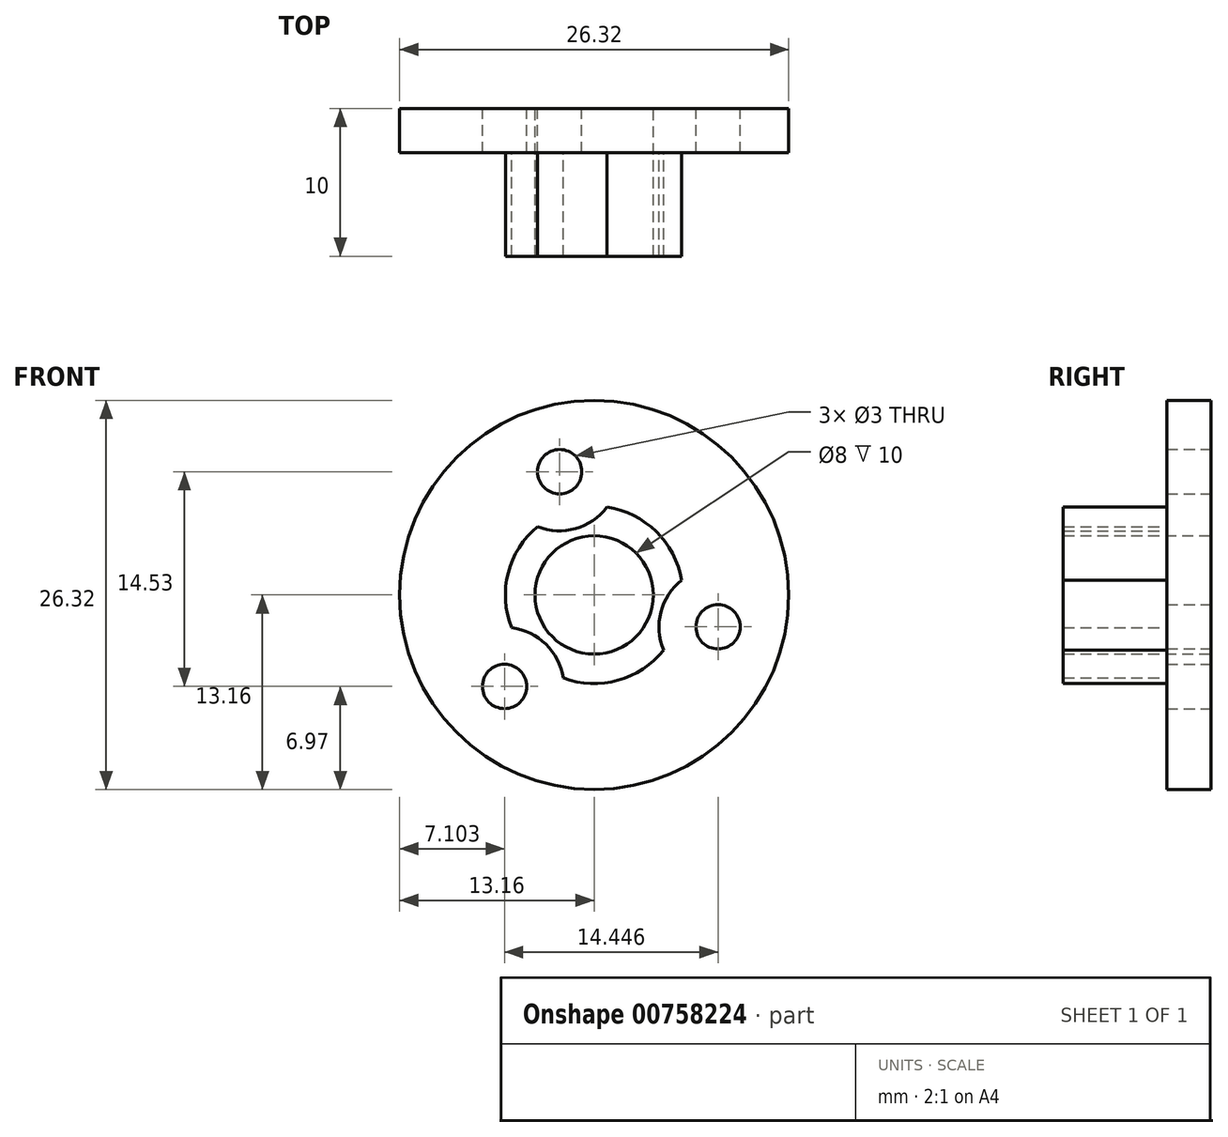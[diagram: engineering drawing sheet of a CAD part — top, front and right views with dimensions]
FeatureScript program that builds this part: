
annotation { "Feature Type Name" : "Feature", "Feature Type Description" : "" }
export const myFeature = defineFeature(function(context is Context, id is Id, definition is map)
    precondition{}
    {
        {
            var Q0;
            Q0=qCreatedBy(makeId("Front.planeOp"),FACE);
            var sketch = newSketch(context, id + "F0", { "sketchPlane" : qUnion([Q0])});
            skCircle(sketch, "E0.cCircle", {"center": v(0, 0) * mm, "radius": 4.33 * mm, "construction": true});
            skLineSegment(sketch, "E0.0", {"start": v(-2.33, 8.34) * mm, "end": v(8.39, -2.15) * mm, "construction": true});
            skLineSegment(sketch, "E0.1", {"start": v(8.39, -2.15) * mm, "end": v(-6.06, -6.2) * mm, "construction": true});
            skLineSegment(sketch, "E0.2", {"start": v(-6.06, -6.2) * mm, "end": v(-2.33, 8.34) * mm, "construction": true});
            skPoint(sketch, "E0.0.midPoint", {"position": v(3.03, 3.1) * mm});
            skCircle(sketch, "E1", {"center": v(0, 0) * mm, "radius": 4 * mm});
            skCircle(sketch, "E2", {"center": v(-2.33, 8.34) * mm, "radius": 1.5 * mm});
            skCircle(sketch, "E3", {"center": v(8.39, -2.15) * mm, "radius": 1.5 * mm});
            skCircle(sketch, "E4", {"center": v(-6.06, -6.2) * mm, "radius": 1.5 * mm});
            skCircle(sketch, "E5", {"center": v(0, 0) * mm, "radius": 13.16 * mm});
            skSolve(sketch);
        }
        {
            var Q0;
            Q0 = qSketchRegion(id + "F0", true);
            extrude(context, id + "F1", {"entities" : qUnion([Q0]), "depth" : 3 * mm, "offsetDistance" : 25 * mm});
        }
        {
            var Q0;
            Q0=makeQuery(id+"F1.opExtrude","CAP_FACE",FACE,{"disambiguationData":[OSD([sQuery(id+"F0.wireOp",EDGE,"E1"),sQuery(id+"F0.wireOp",EDGE,"E2"),sQuery(id+"F0.wireOp",EDGE,"E3"),sQuery(id+"F0.wireOp",EDGE,"E4"),sQuery(id+"F0.wireOp",EDGE,"E5")])],"isStart":false});
            var sketch = newSketch(context, id + "F2", { "sketchPlane" : qUnion([Q0])});
            skCircle(sketch, "E6", {"center": v(0, 0) * mm, "radius": 4 * mm});
            skCircle(sketch, "E7", {"center": v(0, 0) * mm, "radius": 6 * mm});
            skSolve(sketch);
        }
        {
            var Q0;
            Q0 = qSketchRegion(id + "F2", true);
            extrude(context, id + "F3", {"entities" : qUnion([Q0]), "operationType" : NewBodyOperationType.ADD, "depth" : 7 * mm, "offsetDistance" : 25 * mm});
        }
        {
            var Q0;
            Q0=makeQuery(id+"F1.opExtrude","CAP_FACE",FACE,{"disambiguationData":[OSD([sQuery(id+"F0.wireOp",EDGE,"E1"),sQuery(id+"F0.wireOp",EDGE,"E2"),sQuery(id+"F0.wireOp",EDGE,"E3"),sQuery(id+"F0.wireOp",EDGE,"E4"),sQuery(id+"F0.wireOp",EDGE,"E5")])],"isStart":false});
            var sketch = newSketch(context, id + "F4", { "sketchPlane" : qUnion([Q0])});
            skCircle(sketch, "E8", {"center": v(-2.33, 8.34) * mm, "radius": 4 * mm});
            skCircle(sketch, "E9", {"center": v(8.39, -2.15) * mm, "radius": 4 * mm});
            skCircle(sketch, "E10", {"center": v(-6.06, -6.2) * mm, "radius": 4 * mm});
            skSolve(sketch);
        }
        {
            var Q0;
            Q0 = qSketchRegion(id + "F4", true);
            extrude(context, id + "F5", {"entities" : qUnion([Q0]), "operationType" : NewBodyOperationType.REMOVE, "depth" : 25 * mm, "offsetDistance" : 25 * mm});
        }
    });
